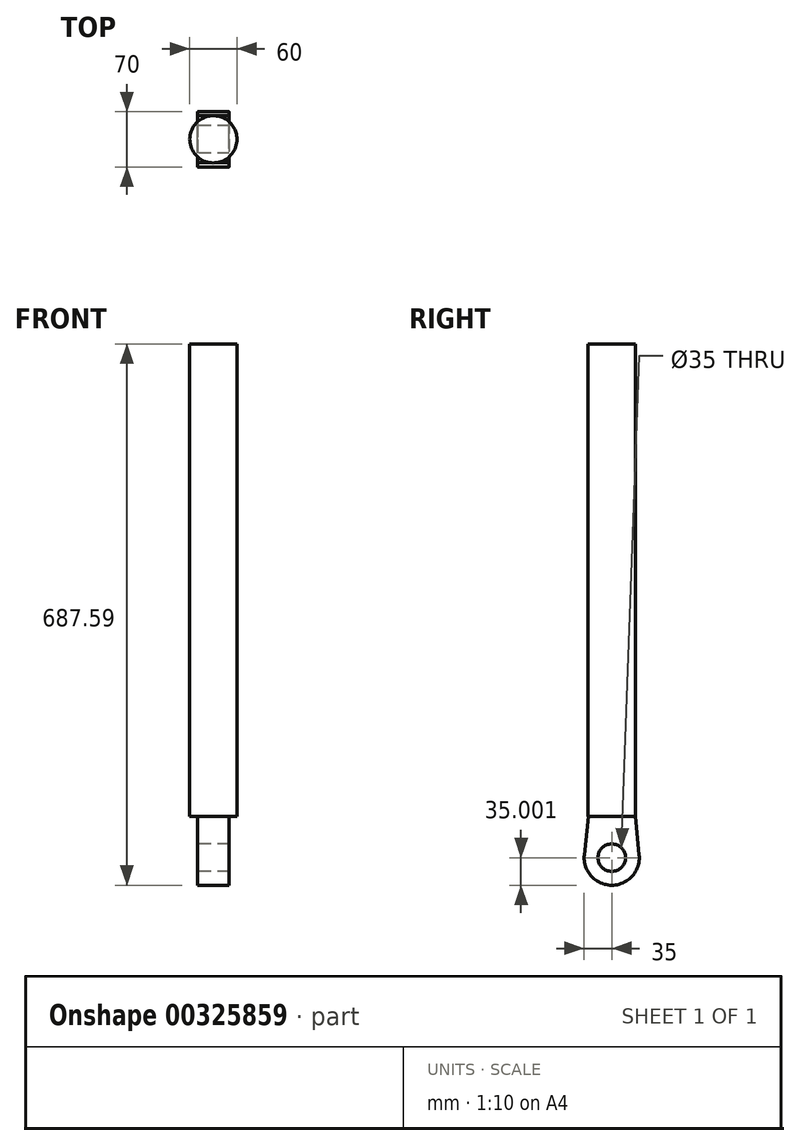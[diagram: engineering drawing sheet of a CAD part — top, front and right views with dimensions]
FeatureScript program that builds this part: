
annotation { "Feature Type Name" : "Feature", "Feature Type Description" : "" }
export const myFeature = defineFeature(function(context is Context, id is Id, definition is map)
    precondition{}
    {
        {
            var Q0;
            Q0=qCreatedBy(makeId("Top.planeOp"),FACE);
            var sketch = newSketch(context, id + "F0", { "sketchPlane" : qUnion([Q0])});
            skCircle(sketch, "E0", {"center": v(0, 0) * mm, "radius": 30 * mm});
            skSolve(sketch);
        }
        {
            var Q0;
            Q0 = qSketchRegion(id + "F0", true);
            extrude(context, id + "F1", {"entities" : qUnion([Q0]), "depth" : 600 * mm});
        }
        {
            var Q0;
            Q0=qCreatedBy(makeId("Right.planeOp"),FACE);
            var sketch = newSketch(context, id + "F2", { "sketchPlane" : qUnion([Q0])});
            skArc(sketch, "E1", {"start": v(-34.82, -49.04) * mm, "mid": v(-0.12, -87.59) * mm, "end": v(34.84, -49.29) * mm});
            skLineSegment(sketch, "E2", {"start": v(30.17, 0) * mm, "end": v(34.84, -49.29) * mm});
            skLineSegment(sketch, "E3", {"start": v(-29.83, 0) * mm, "end": v(-34.82, -49.04) * mm});
            skLineSegment(sketch, "E4", {"start": v(30.17, 0) * mm, "end": v(-29.83, 0) * mm});
            skSolve(sketch);
        }
        {
            var Q0;
            Q0=makeQuery(id+"F2.imprint","IMPRINT",FACE,{"disambiguationData":[TD([[makeQuery(id+"F2.imprint","IMPRINT",EDGE,{"derivedFrom":sQuery(id+"F2.wireOp",EDGE,"E1")}),1.0]])]});
            extrude(context, id + "F3", {"entities" : qUnion([Q0]), "operationType" : NewBodyOperationType.ADD, "endBound" : BoundingType.SYMMETRIC, "depth" : 40 * mm});
        }
        {
            var Q0;
            Q0=makeQuery(id+"F3.opExtrude","CAP_FACE",FACE,{"disambiguationData":[OSD([sQuery(id+"F2.wireOp",EDGE,"E1"),sQuery(id+"F2.wireOp",EDGE,"E2"),sQuery(id+"F2.wireOp",EDGE,"E3"),sQuery(id+"F2.wireOp",EDGE,"E4")])],"isStart":true});
            var sketch = newSketch(context, id + "F4", { "sketchPlane" : qUnion([Q0])});
            skCircle(sketch, "E5", {"center": v(0, -52.59) * mm, "radius": 17.5 * mm});
            skSolve(sketch);
        }
        {
            var Q0;
            Q0=makeQuery(id+"F4.imprint","IMPRINT",FACE,{"disambiguationData":[TD([[makeQuery(id+"F4.imprint","IMPRINT",EDGE,{"derivedFrom":sQuery(id+"F4.wireOp",EDGE,"E5")}),1.0]])]});
            extrude(context, id + "F5", {"entities" : qUnion([Q0]), "operationType" : NewBodyOperationType.REMOVE, "oppositeDirection" : true, "depth" : 50 * mm});
        }
    });
